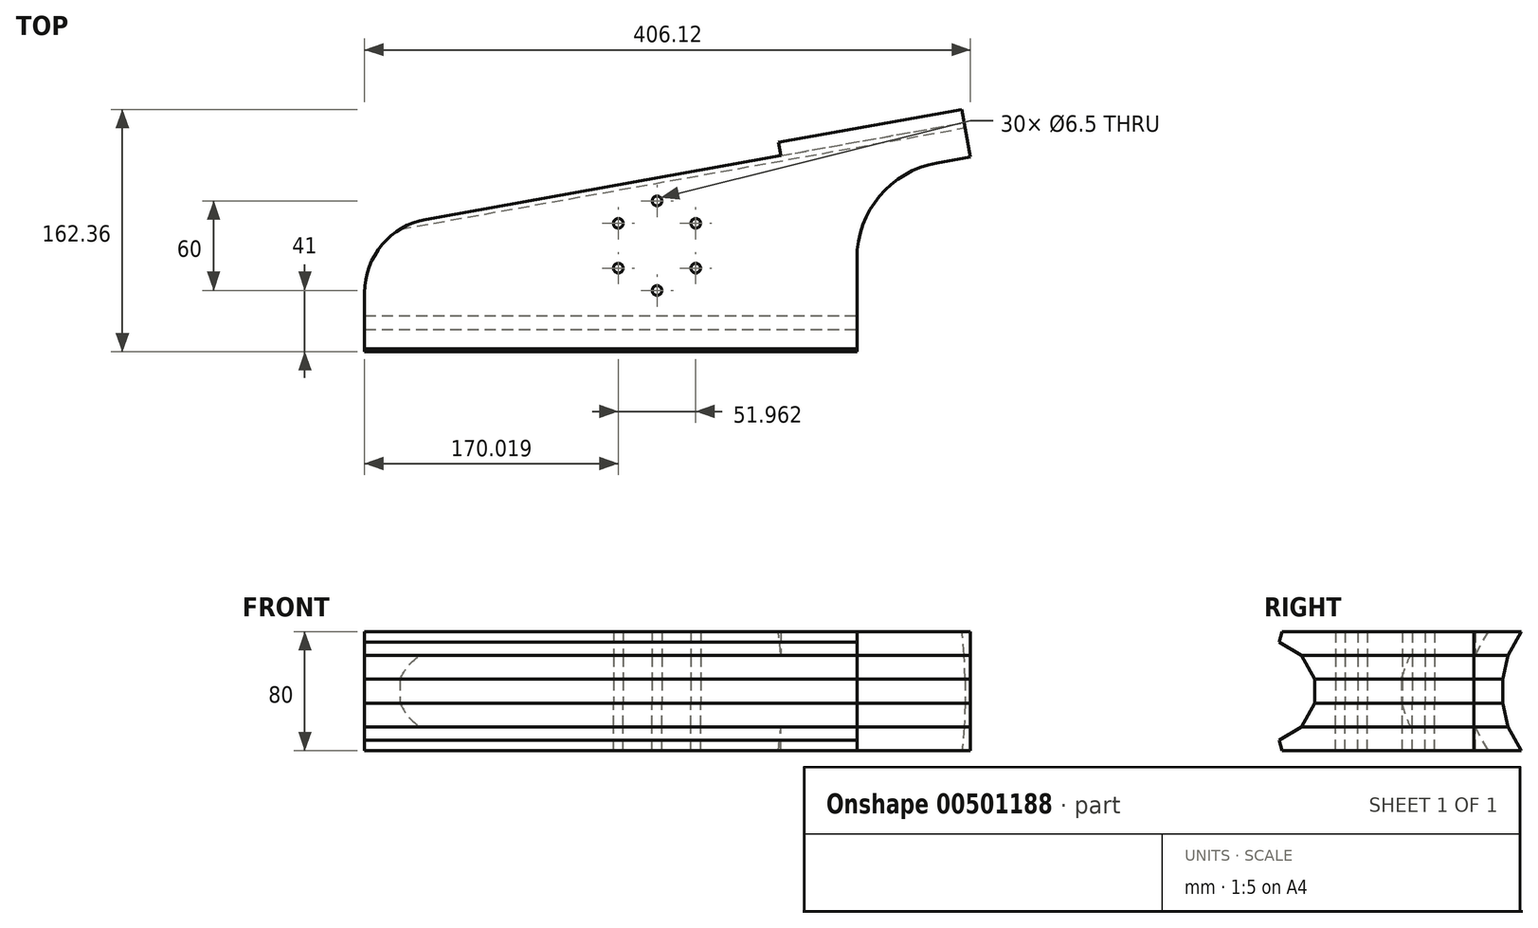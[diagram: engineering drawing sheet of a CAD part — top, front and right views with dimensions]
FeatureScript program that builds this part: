
annotation { "Feature Type Name" : "Feature", "Feature Type Description" : "" }
export const myFeature = defineFeature(function(context is Context, id is Id, definition is map)
    precondition{}
    {
        {
            var Q0;
            Q0=qCreatedBy(makeId("Top.planeOp"),FACE);
            var sketch = newSketch(context, id + "F0", { "sketchPlane" : qUnion([Q0])});
            skLineSegment(sketch, "E0", {"start": v(-50, 0) * mm, "end": v(280, 0) * mm});
            skLineSegment(sketch, "E1", {"start": v(-50, 0) * mm, "end": v(-50, 39.5) * mm});
            skLineSegment(sketch, "E2", {"start": v(280, 0) * mm, "end": v(352, 0) * mm, "construction": true});
            skLineSegment(sketch, "E3", {"start": v(352, 0) * mm, "end": v(352, 153.5) * mm, "construction": true});
            skLineSegment(sketch, "E4", {"start": v(228.97, 131.4) * mm, "end": v(-8.84, 88.71) * mm});
            skArc(sketch, "E5", {"start": v(-8.84, 88.71) * mm, "mid": v(-38.35, 71.58) * mm, "end": v(-50, 39.5) * mm});
            skArc(sketch, "E6", {"start": v(333.51, 126.48) * mm, "mid": v(295.14, 104.2) * mm, "end": v(280, 62.5) * mm});
            skLineSegment(sketch, "E7", {"start": v(280, 0) * mm, "end": v(280, 62.5) * mm});
            skLineSegment(sketch, "E8", {"start": v(352, 153.5) * mm, "end": v(356.12, 130.54) * mm});
            skLineSegment(sketch, "E9", {"start": v(356.12, 130.54) * mm, "end": v(333.51, 126.48) * mm});
            skLineSegment(sketch, "E10", {"start": v(352, 153.5) * mm, "end": v(350.4, 162.36) * mm});
            skLineSegment(sketch, "E11", {"start": v(350.4, 162.36) * mm, "end": v(227.38, 140.27) * mm});
            skLineSegment(sketch, "E12", {"start": v(227.38, 140.27) * mm, "end": v(228.97, 131.4) * mm});
            skLineSegment(sketch, "E13", {"start": v(77.77, 71) * mm, "end": v(199.65, 71) * mm, "construction": true});
            skLineSegment(sketch, "E14", {"start": v(146, 76.85) * mm, "end": v(146, 19.8) * mm, "construction": true});
            skCircle(sketch, "E15", {"center": v(146, 71) * mm, "radius": 30 * mm, "construction": true});
            skCircle(sketch, "E16", {"center": v(146, 41) * mm, "radius": 3.25 * mm});
            skCircle(sketch, "E17.1.0", {"center": v(171.98, 56) * mm, "radius": 3.25 * mm});
            skCircle(sketch, "E17.2.0", {"center": v(171.98, 86) * mm, "radius": 3.25 * mm});
            skCircle(sketch, "E17.3.0", {"center": v(146, 101) * mm, "radius": 3.25 * mm});
            skCircle(sketch, "E17.4.0", {"center": v(120.02, 86) * mm, "radius": 3.25 * mm});
            skCircle(sketch, "E17.5.0", {"center": v(120.02, 56) * mm, "radius": 3.25 * mm});
            skSolve(sketch);
        }
        {
            var Q0;
            Q0 = qSketchRegion(id + "F0", true);
            extrude(context, id + "F1", {"entities" : qUnion([Q0]), "endBound" : BoundingType.SYMMETRIC, "depth" : 16 * mm});
        }
        {
            var Q0;
            Q0=makeQuery(id+"F1.opExtrude","CAP_FACE",FACE,{"disambiguationData":[OSD([sQuery(id+"F0.wireOp",EDGE,"E0"),sQuery(id+"F0.wireOp",EDGE,"E1"),sQuery(id+"F0.wireOp",EDGE,"E4"),sQuery(id+"F0.wireOp",EDGE,"E5"),sQuery(id+"F0.wireOp",EDGE,"E6"),sQuery(id+"F0.wireOp",EDGE,"E7"),sQuery(id+"F0.wireOp",EDGE,"E8"),sQuery(id+"F0.wireOp",EDGE,"E9"),sQuery(id+"F0.wireOp",EDGE,"E10"),sQuery(id+"F0.wireOp",EDGE,"E11"),sQuery(id+"F0.wireOp",EDGE,"E12"),sQuery(id+"F0.wireOp",EDGE,"E16"),sQuery(id+"F0.wireOp",EDGE,"E17.1.0"),sQuery(id+"F0.wireOp",EDGE,"E17.2.0"),sQuery(id+"F0.wireOp",EDGE,"E17.3.0"),sQuery(id+"F0.wireOp",EDGE,"E17.4.0"),sQuery(id+"F0.wireOp",EDGE,"E17.5.0")])],"isStart":false});
            extrude(context, id + "F2", {"entities" : qUnion([Q0]), "depth" : 16 * mm});
        }
        {
            var Q0;
            Q0=makeQuery(id+"F2.opExtrude","CAP_FACE",FACE,{"disambiguationData":[OSD([sQuery(id+"F0.wireOp",EDGE,"E0"),sQuery(id+"F0.wireOp",EDGE,"E1"),sQuery(id+"F0.wireOp",EDGE,"E4"),sQuery(id+"F0.wireOp",EDGE,"E5"),sQuery(id+"F0.wireOp",EDGE,"E6"),sQuery(id+"F0.wireOp",EDGE,"E7"),sQuery(id+"F0.wireOp",EDGE,"E8"),sQuery(id+"F0.wireOp",EDGE,"E9"),sQuery(id+"F0.wireOp",EDGE,"E10"),sQuery(id+"F0.wireOp",EDGE,"E11"),sQuery(id+"F0.wireOp",EDGE,"E12"),sQuery(id+"F0.wireOp",EDGE,"E16"),sQuery(id+"F0.wireOp",EDGE,"E17.1.0"),sQuery(id+"F0.wireOp",EDGE,"E17.2.0"),sQuery(id+"F0.wireOp",EDGE,"E17.3.0"),sQuery(id+"F0.wireOp",EDGE,"E17.4.0"),sQuery(id+"F0.wireOp",EDGE,"E17.5.0")])],"isStart":false});
            extrude(context, id + "F3", {"entities" : qUnion([Q0]), "depth" : 16 * mm});
        }
        {
            var Q0;
            Q0=makeQuery(id+"F1.opExtrude","CAP_FACE",FACE,{"disambiguationData":[OSD([sQuery(id+"F0.wireOp",EDGE,"E0"),sQuery(id+"F0.wireOp",EDGE,"E1"),sQuery(id+"F0.wireOp",EDGE,"E4"),sQuery(id+"F0.wireOp",EDGE,"E5"),sQuery(id+"F0.wireOp",EDGE,"E6"),sQuery(id+"F0.wireOp",EDGE,"E7"),sQuery(id+"F0.wireOp",EDGE,"E8"),sQuery(id+"F0.wireOp",EDGE,"E9"),sQuery(id+"F0.wireOp",EDGE,"E10"),sQuery(id+"F0.wireOp",EDGE,"E11"),sQuery(id+"F0.wireOp",EDGE,"E12"),sQuery(id+"F0.wireOp",EDGE,"E16"),sQuery(id+"F0.wireOp",EDGE,"E17.1.0"),sQuery(id+"F0.wireOp",EDGE,"E17.2.0"),sQuery(id+"F0.wireOp",EDGE,"E17.3.0"),sQuery(id+"F0.wireOp",EDGE,"E17.4.0"),sQuery(id+"F0.wireOp",EDGE,"E17.5.0")])],"isStart":true});
            extrude(context, id + "F4", {"entities" : qUnion([Q0]), "depth" : 16 * mm});
        }
        {
            var Q0;
            Q0=makeQuery(id+"F4.opExtrude","CAP_FACE",FACE,{"disambiguationData":[OSD([sQuery(id+"F0.wireOp",EDGE,"E0"),sQuery(id+"F0.wireOp",EDGE,"E1"),sQuery(id+"F0.wireOp",EDGE,"E4"),sQuery(id+"F0.wireOp",EDGE,"E5"),sQuery(id+"F0.wireOp",EDGE,"E6"),sQuery(id+"F0.wireOp",EDGE,"E7"),sQuery(id+"F0.wireOp",EDGE,"E8"),sQuery(id+"F0.wireOp",EDGE,"E9"),sQuery(id+"F0.wireOp",EDGE,"E10"),sQuery(id+"F0.wireOp",EDGE,"E11"),sQuery(id+"F0.wireOp",EDGE,"E12"),sQuery(id+"F0.wireOp",EDGE,"E16"),sQuery(id+"F0.wireOp",EDGE,"E17.1.0"),sQuery(id+"F0.wireOp",EDGE,"E17.2.0"),sQuery(id+"F0.wireOp",EDGE,"E17.3.0"),sQuery(id+"F0.wireOp",EDGE,"E17.4.0"),sQuery(id+"F0.wireOp",EDGE,"E17.5.0")])],"isStart":false});
            extrude(context, id + "F5", {"entities" : qUnion([Q0]), "depth" : 16 * mm});
        }
        {
            var Q0;
            Q0=makeQuery(id+"F1.opExtrude","SWEPT_FACE",FACE,{"disambiguationData":[OSD([sQuery(id+"F0.wireOp",EDGE,"E7")])]});
            var sketch = newSketch(context, id + "F6", { "sketchPlane" : qUnion([Q0])});
            skLineSegment(sketch, "E18", {"start": v(24, 8) * mm, "end": v(24, -8) * mm});
            skLineSegment(sketch, "E19.0.2", {"start": v(2, 40) * mm, "end": v(0, 40) * mm});
            skLineSegment(sketch, "E19.0.3", {"start": v(0, 33) * mm, "end": v(0, 24) * mm});
            skLineSegment(sketch, "E20", {"start": v(24, 8) * mm, "end": v(15, 24) * mm});
            skLineSegment(sketch, "E21", {"start": v(15, 24) * mm, "end": v(0, 33) * mm});
            skLineSegment(sketch, "E22.MirrorCS", {"start": v(24, -8) * mm, "end": v(15, -24) * mm});
            skLineSegment(sketch, "E23.MirrorCS", {"start": v(15, -24) * mm, "end": v(0, -33) * mm});
            skLineSegment(sketch, "E24", {"start": v(0, 33) * mm, "end": v(2, 40) * mm});
            skLineSegment(sketch, "E25.MirrorCS", {"start": v(0, -33) * mm, "end": v(2, -40) * mm});
            skLineSegment(sketch, "E26.MirrorCS", {"start": v(2, -40) * mm, "end": v(0, -40) * mm});
            skPoint(sketch, "E27.0.3.end.orphan", {"position": v(62.5, -24) * mm});
            skPoint(sketch, "E27.0.3.start.orphan", {"position": v(62.5, -40) * mm});
            skPoint(sketch, "E28.0.3.end.orphan", {"position": v(62.5, -8) * mm});
            skPoint(sketch, "E29.0.1.start.orphan", {"position": v(62.5, 8) * mm});
            skPoint(sketch, "E19.0.1.end.orphan", {"position": v(62.5, 40) * mm});
            skPoint(sketch, "E28.0.1.end.orphan", {"position": v(0, -24) * mm});
            skPoint(sketch, "E28.0.1.start.orphan", {"position": v(0, -8) * mm});
            skPoint(sketch, "E29.0.3.end.orphan", {"position": v(0, 8) * mm});
            skPoint(sketch, "E29.0.3.start.orphan", {"position": v(0, 24) * mm});
            skPoint(sketch, "E27.0.1.end.orphan", {"position": v(0, -40) * mm});
            skLineSegment(sketch, "E30", {"start": v(0, 40) * mm, "end": v(0, -40) * mm});
            skSolve(sketch);
        }
        {
            var Q0;
            Q0 = qSketchRegion(id + "F6", true);
            extrude(context, id + "F7", {"entities" : qUnion([Q0]), "operationType" : NewBodyOperationType.REMOVE, "endBound" : BoundingType.THROUGH_ALL, "oppositeDirection" : true, "depth" : 25 * mm});
        }
        {
            var Q0;
            Q0=makeQuery(id+"F1.opExtrude","SWEPT_FACE",FACE,{"disambiguationData":[OSD([sQuery(id+"F0.wireOp",EDGE,"E8"),sQuery(id+"F0.wireOp",EDGE,"E10")])]});
            var sketch = newSketch(context, id + "F8", { "sketchPlane" : qUnion([Q0])});
            skLineSegment(sketch, "E31", {"start": v(85.38, 8) * mm, "end": v(85.38, -8) * mm});
            skLineSegment(sketch, "E32", {"start": v(85.38, -8) * mm, "end": v(88.88, -24.12) * mm});
            skLineSegment(sketch, "E33", {"start": v(88.88, -24.12) * mm, "end": v(97.88, -40) * mm});
            skPoint(sketch, "E34.endSnap0", {"position": v(85.38, 0) * mm});
            skLineSegment(sketch, "E35.MirrorCS", {"start": v(85.38, 8) * mm, "end": v(88.88, 24.12) * mm});
            skLineSegment(sketch, "E36.MirrorCS", {"start": v(88.88, 24.12) * mm, "end": v(97.88, 40) * mm});
            skLineSegment(sketch, "E37", {"start": v(97.88, 40) * mm, "end": v(97.88, -40) * mm});
            skPoint(sketch, "E38.0.start.orphan", {"position": v(65.55, -40) * mm});
            skPoint(sketch, "E39.orphan", {"position": v(75.4, 0) * mm});
            skPoint(sketch, "E34.start.orphan", {"position": v(97.88, 0) * mm});
            skSolve(sketch);
        }
        {
            var Q0;
            Q0 = qSketchRegion(id + "F8", true);
            extrude(context, id + "F9", {"entities" : qUnion([Q0]), "operationType" : NewBodyOperationType.REMOVE, "endBound" : BoundingType.THROUGH_ALL, "oppositeDirection" : true, "depth" : 25 * mm});
        }
    });
